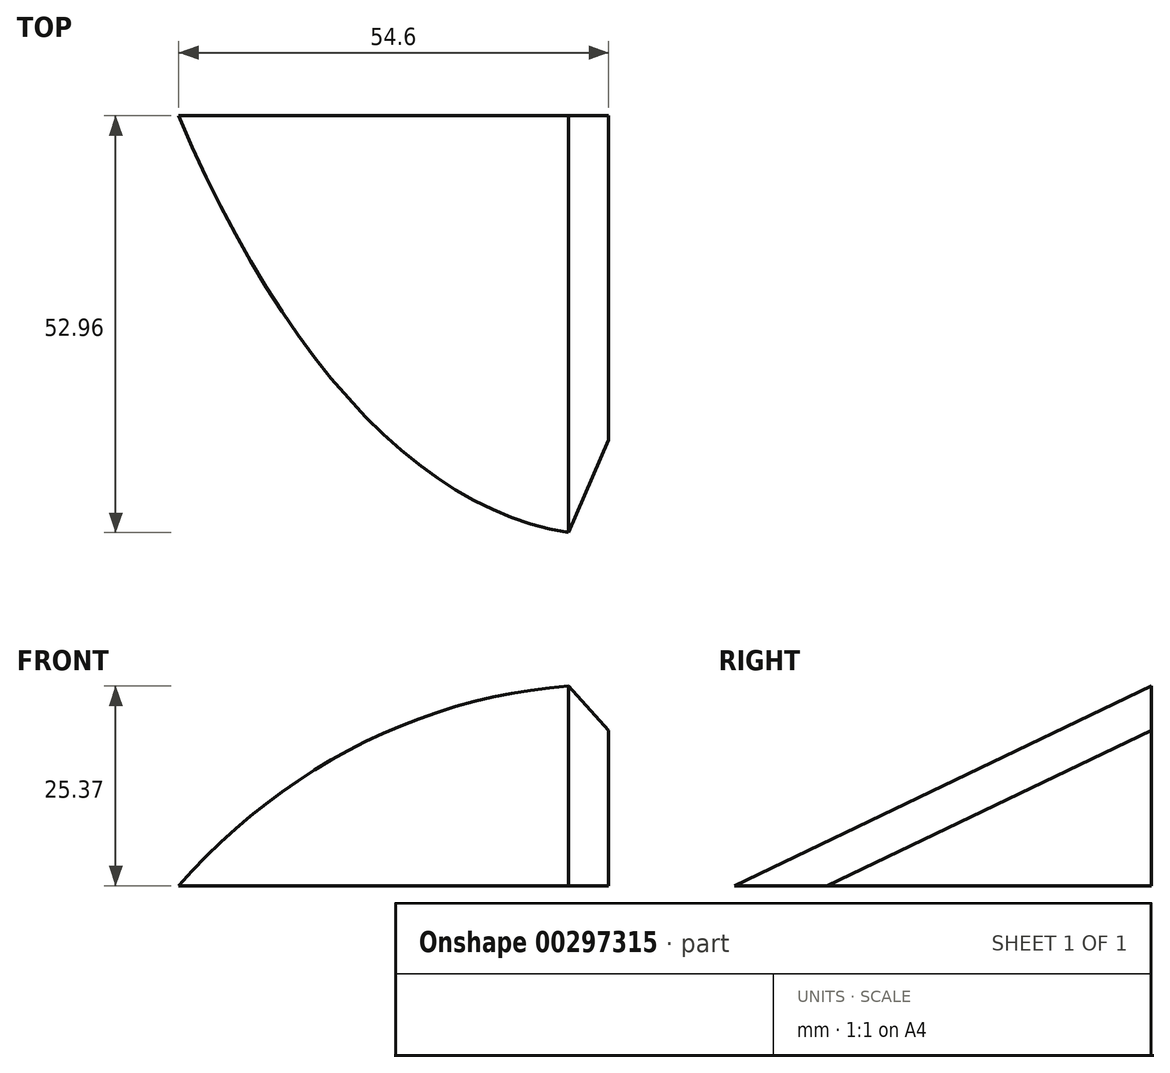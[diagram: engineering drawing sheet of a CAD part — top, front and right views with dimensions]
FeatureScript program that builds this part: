
annotation { "Feature Type Name" : "Feature", "Feature Type Description" : "" }
export const myFeature = defineFeature(function(context is Context, id is Id, definition is map)
    precondition{}
    {
        {
            var Q0;
            Q0=qCreatedBy(makeId("Top.planeOp"),FACE);
            var sketch = newSketch(context, id + "F0", { "sketchPlane" : qUnion([Q0])});
            skLineSegment(sketch, "E0", {"start": v(0, 0) * mm, "end": v(-58.72, 0) * mm});
            skLineSegment(sketch, "E1", {"start": v(-58.72, 0) * mm, "end": v(-48.44, 24.9) * mm});
            skLineSegment(sketch, "E2", {"start": v(-48.44, 24.9) * mm, "end": v(-3.5, 24.9) * mm});
            skLineSegment(sketch, "E3", {"start": v(-3.5, 24.9) * mm, "end": v(0, 0) * mm});
            skSolve(sketch);
        }
        {
            var Q0;
            Q0=sQuery(id+"F0.wireOp",EDGE,"E1");
            var Q1;
            Q1=sQuery(id+"F0.wireOp",EDGE,"E2");
            var Q2;
            Q2=sQuery(id+"F0.wireOp",EDGE,"E3");
            var Q3;
            Q3=sQuery(id+"F0.wireOp",EDGE,"E0");
            extrude(context, id + "F1", {"bodyType" : ToolBodyType.SURFACE, "surfaceEntities" : qUnion([Q0, Q1, Q2, Q3]), "depth" : 25.4 * mm});
        }
        {
            var Q0;
            Q0=qCreatedBy(makeId("Right.planeOp"),FACE);
            var sketch = newSketch(context, id + "F2", { "sketchPlane" : qUnion([Q0])});
            skLineSegment(sketch, "E4", {"start": v(0, 0) * mm, "end": v(0, 25.37) * mm});
            skLineSegment(sketch, "E5", {"start": v(0, 25.37) * mm, "end": v(-52.96, 0) * mm});
            skLineSegment(sketch, "E6", {"start": v(-52.96, 0) * mm, "end": v(0, 0) * mm});
            skSolve(sketch);
        }
        {
            var Q0;
            Q0 = qSketchRegion(id + "F2", true);
            extrude(context, id + "F3", {"entities" : qUnion([Q0]), "oppositeDirection" : true, "depth" : 76.2 * mm});
        }
        {
            var Q0;
            Q0=makeQuery(id+"F3.opExtrude","CAP_EDGE",EDGE,{"disambiguationData":[OSD([sQuery(id+"F2.wireOp",EDGE,"E5")])],"isStart":true});
            chamfer(context, id + "F4", {"entities" : qUnion([Q0]), "width" : 5.08 * mm, "tangentPropagation" : true});
        }
        {
            var Q0;
            Q0=makeQuery(id+"F3.opExtrude","CAP_EDGE",EDGE,{"disambiguationData":[OSD([sQuery(id+"F2.wireOp",EDGE,"E5")])],"isStart":false});
            fillet(context, id + "F5", {"entities" : qUnion([Q0]), "radius" : 76.2 * mm, "tangentPropagation" : true, "allowEdgeOverflow" : false});
        }
        {
            var Q0;
            Q0=makeQuery(id+"F1.opExtrude","SWEPT_EDGE",EDGE,{"disambiguationData":[OSD([sQuery(id+"F0.wireOp",VERTEX,"E0.start")])]});
            chamfer(context, id + "F6", {"entities" : qUnion([Q0]), "width" : 5.08 * mm, "tangentPropagation" : true});
        }
    });
